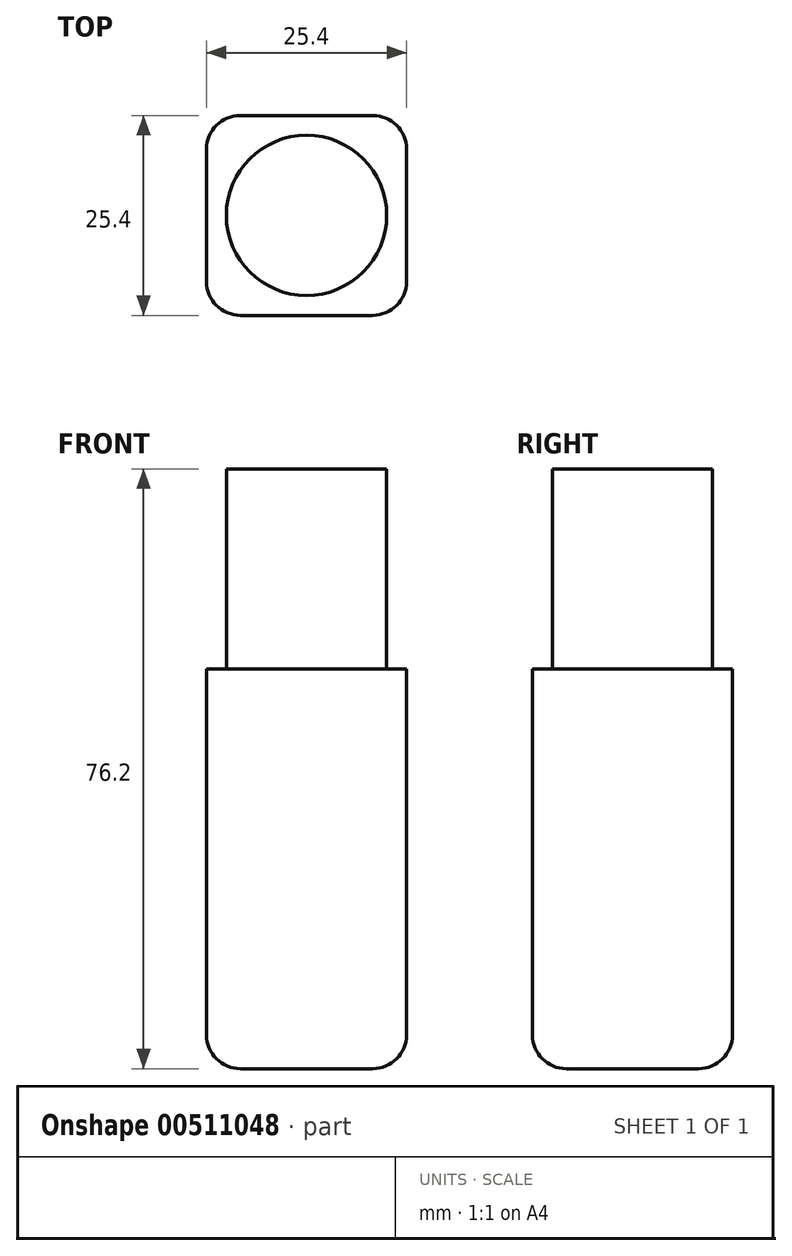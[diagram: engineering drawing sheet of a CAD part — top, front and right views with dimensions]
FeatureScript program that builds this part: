
annotation { "Feature Type Name" : "Feature", "Feature Type Description" : "" }
export const myFeature = defineFeature(function(context is Context, id is Id, definition is map)
    precondition{}
    {
        {
            var Q0;
            Q0=qCreatedBy(makeId("Top.planeOp"),FACE);
            var sketch = newSketch(context, id + "F0", { "sketchPlane" : qUnion([Q0])});
            skLineSegment(sketch, "E0.bottom", {"start": v(12.7, -12.7) * mm, "end": v(-12.7, -12.7) * mm});
            skLineSegment(sketch, "E0.top", {"start": v(12.7, 12.7) * mm, "end": v(-12.7, 12.7) * mm});
            skLineSegment(sketch, "E0.left", {"start": v(12.7, -12.7) * mm, "end": v(12.7, 12.7) * mm});
            skLineSegment(sketch, "E0.right", {"start": v(-12.7, -12.7) * mm, "end": v(-12.7, 12.7) * mm});
            skPoint(sketch, "E0.middle", {"position": v(0, 0) * mm});
            skSolve(sketch);
        }
        {
            var Q0;
            Q0=makeQuery(id+"F0.imprint","IMPRINT",FACE,{"disambiguationData":[TD([[makeQuery(id+"F0.imprint","IMPRINT",EDGE,{"derivedFrom":sQuery(id+"F0.wireOp",EDGE,"E0.bottom")}),-1.0]])]});
            extrude(context, id + "F1", {"entities" : qUnion([Q0]), "depth" : 50.8 * mm});
        }
        {
            var Q0;
            Q0=makeQuery(id+"F1.opExtrude","SWEPT_EDGE",EDGE,{"disambiguationData":[OSD([sQuery(id+"F0.wireOp",EDGE,"E0.bottom"),sQuery(id+"F0.wireOp",EDGE,"E0.left")])]});
            var Q1;
            Q1=makeQuery(id+"F1.opExtrude","SWEPT_EDGE",EDGE,{"disambiguationData":[OSD([sQuery(id+"F0.wireOp",EDGE,"E0.top"),sQuery(id+"F0.wireOp",EDGE,"E0.left")])]});
            var Q2;
            Q2=makeQuery(id+"F1.opExtrude","SWEPT_EDGE",EDGE,{"disambiguationData":[OSD([sQuery(id+"F0.wireOp",EDGE,"E0.bottom"),sQuery(id+"F0.wireOp",EDGE,"E0.right")])]});
            var Q3;
            Q3=makeQuery(id+"F1.opExtrude","SWEPT_EDGE",EDGE,{"disambiguationData":[OSD([sQuery(id+"F0.wireOp",EDGE,"E0.top"),sQuery(id+"F0.wireOp",EDGE,"E0.right")])]});
            var Q4;
            Q4=makeQuery(id+"F1.opExtrude","CAP_EDGE",EDGE,{"disambiguationData":[OSD([sQuery(id+"F0.wireOp",EDGE,"E0.top")])],"isStart":true});
            var Q5;
            Q5=makeQuery(id+"F1.opExtrude","CAP_EDGE",EDGE,{"disambiguationData":[OSD([sQuery(id+"F0.wireOp",EDGE,"E0.right")])],"isStart":true});
            var Q6;
            Q6=makeQuery(id+"F1.opExtrude","CAP_EDGE",EDGE,{"disambiguationData":[OSD([sQuery(id+"F0.wireOp",EDGE,"E0.bottom")])],"isStart":true});
            var Q7;
            Q7=makeQuery(id+"F1.opExtrude","CAP_EDGE",EDGE,{"disambiguationData":[OSD([sQuery(id+"F0.wireOp",EDGE,"E0.left")])],"isStart":true});
            fillet(context, id + "F2", {"entities" : qUnion([Q0, Q1, Q2, Q3, Q4, Q5, Q6, Q7]), "radius" : 4.3 * mm, "tangentPropagation" : true, "allowEdgeOverflow" : false});
        }
        {
            var Q0;
            Q0=makeQuery(id+"F1.opExtrude","CAP_FACE",FACE,{"disambiguationData":[OSD([sQuery(id+"F0.wireOp",EDGE,"E0.bottom"),sQuery(id+"F0.wireOp",EDGE,"E0.top"),sQuery(id+"F0.wireOp",EDGE,"E0.left"),sQuery(id+"F0.wireOp",EDGE,"E0.right")])],"isStart":false});
            var sketch = newSketch(context, id + "F3", { "sketchPlane" : qUnion([Q0])});
            skCircle(sketch, "E1", {"center": v(0, 0) * mm, "radius": 10.18 * mm});
            skSolve(sketch);
        }
        {
            var Q0;
            Q0=makeQuery(id+"F3.imprint","IMPRINT",FACE,{"disambiguationData":[TD([[makeQuery(id+"F3.imprint","IMPRINT",EDGE,{"derivedFrom":sQuery(id+"F3.wireOp",EDGE,"E1")}),1.0]])]});
            extrude(context, id + "F4", {"entities" : qUnion([Q0]), "operationType" : NewBodyOperationType.ADD, "depth" : 25.4 * mm});
        }
    });
